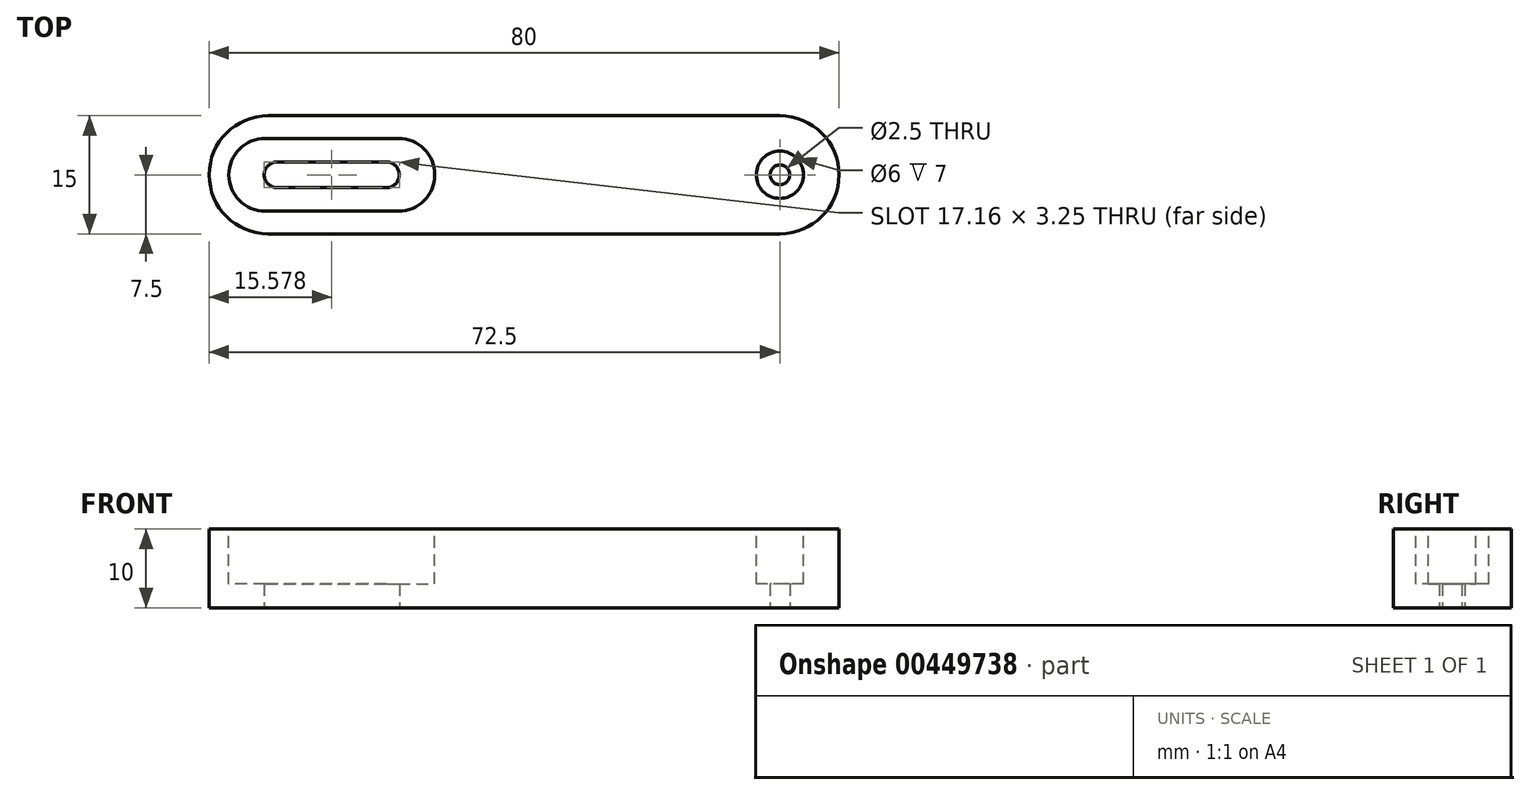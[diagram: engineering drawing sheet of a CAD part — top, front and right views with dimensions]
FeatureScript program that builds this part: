
annotation { "Feature Type Name" : "Feature", "Feature Type Description" : "" }
export const myFeature = defineFeature(function(context is Context, id is Id, definition is map)
    precondition{}
    {
        {
            var Q0;
            Q0=qCreatedBy(makeId("Top.planeOp"),FACE);
            var sketch = newSketch(context, id + "F0", { "sketchPlane" : qUnion([Q0])});
            skLineSegment(sketch, "E0.bottom", {"start": v(32.5, 7.5) * mm, "end": v(-32.5, 7.5) * mm});
            skLineSegment(sketch, "E0.top", {"start": v(32.5, -7.5) * mm, "end": v(-32.5, -7.5) * mm});
            skPoint(sketch, "E0.middle", {"position": v(0, 0) * mm});
            skCircle(sketch, "E1", {"center": v(32.5, 0) * mm, "radius": 1.25 * mm});
            skArc(sketch, "E2", {"start": v(-32.5, -7.5) * mm, "mid": v(-40, 0) * mm, "end": v(-32.5, 7.5) * mm});
            skArc(sketch, "E3", {"start": v(32.5, -7.5) * mm, "mid": v(40, 0) * mm, "end": v(32.5, 7.5) * mm});
            skLineSegment(sketch, "E4.bottom", {"start": v(-17.47, -1.63) * mm, "end": v(-31.38, -1.63) * mm});
            skLineSegment(sketch, "E4.top", {"start": v(-17.47, 1.62) * mm, "end": v(-31.38, 1.63) * mm});
            skPoint(sketch, "E4.middle", {"position": v(-24.42, 0) * mm});
            skArc(sketch, "E5", {"start": v(-31.38, -1.63) * mm, "mid": v(-33, 0) * mm, "end": v(-31.38, 1.63) * mm});
            skArc(sketch, "E6", {"start": v(-17.47, -1.63) * mm, "mid": v(-15.84, 0) * mm, "end": v(-17.47, 1.62) * mm});
            skSolve(sketch);
        }
        {
            var Q0;
            Q0 = qSketchRegion(id + "F0", true);
            extrude(context, id + "F1", {"entities" : qUnion([Q0]), "depth" : 10 * mm});
        }
        {
            var Q0;
            Q0=makeQuery(id+"F1.opExtrude","CAP_FACE",FACE,{"disambiguationData":[OSD([sQuery(id+"F0.wireOp",EDGE,"E0.bottom"),sQuery(id+"F0.wireOp",EDGE,"E0.top"),sQuery(id+"F0.wireOp",EDGE,"E1"),sQuery(id+"F0.wireOp",EDGE,"E2"),sQuery(id+"F0.wireOp",EDGE,"E3"),sQuery(id+"F0.wireOp",EDGE,"E4.bottom"),sQuery(id+"F0.wireOp",EDGE,"E4.top"),sQuery(id+"F0.wireOp",EDGE,"E5"),sQuery(id+"F0.wireOp",EDGE,"E6")])],"isStart":false});
            cPlane(context, id + "F2", {"entities" : qUnion([Q0]), "cplaneType" : CPlaneType.OFFSET, "offset" : 0 * mm, "width" : 150 * mm, "height" : 150 * mm});
        }
        {
            var Q0;
            Q0=qCreatedBy(id+"F2.planeOp",FACE);
            var sketch = newSketch(context, id + "F3", { "sketchPlane" : qUnion([Q0])});
            skCircle(sketch, "E7.0", {"center": v(32.5, 0) * mm, "radius": 1.25 * mm, "construction": true});
            skArc(sketch, "E8.0", {"start": v(-17.47, -1.63) * mm, "mid": v(-15.84, 0) * mm, "end": v(-17.47, 1.62) * mm, "construction": true});
            skLineSegment(sketch, "E9.0", {"start": v(-17.47, -1.63) * mm, "end": v(-31.38, -1.63) * mm, "construction": true});
            skArc(sketch, "E10.0", {"start": v(-31.38, -1.63) * mm, "mid": v(-33, 0) * mm, "end": v(-31.38, 1.63) * mm, "construction": true});
            skLineSegment(sketch, "E11.0", {"start": v(-17.47, 1.62) * mm, "end": v(-31.38, 1.63) * mm, "construction": true});
            skCircle(sketch, "E12", {"center": v(32.5, 0) * mm, "radius": 3 * mm});
            skLineSegment(sketch, "E13.bottom", {"start": v(-32.88, 4.62) * mm, "end": v(-15.97, 4.62) * mm});
            skLineSegment(sketch, "E13.top", {"start": v(-32.88, -4.63) * mm, "end": v(-15.97, -4.63) * mm});
            skLineSegment(sketch, "E13.left", {"start": v(-32.88, 4.62) * mm, "end": v(-32.88, -4.63) * mm});
            skLineSegment(sketch, "E13.right", {"start": v(-15.97, 4.63) * mm, "end": v(-15.97, -4.63) * mm});
            skArc(sketch, "E14", {"start": v(-15.97, -4.63) * mm, "mid": v(-11.34, 0) * mm, "end": v(-15.97, 4.63) * mm});
            skArc(sketch, "E15", {"start": v(-32.88, -4.63) * mm, "mid": v(-37.5, 0) * mm, "end": v(-32.88, 4.62) * mm});
            skSolve(sketch);
        }
        {
            var Q0;
            Q0 = qSketchRegion(id + "F3", true);
            extrude(context, id + "F4", {"entities" : qUnion([Q0]), "operationType" : NewBodyOperationType.REMOVE, "oppositeDirection" : true, "depth" : 7 * mm});
        }
    });
